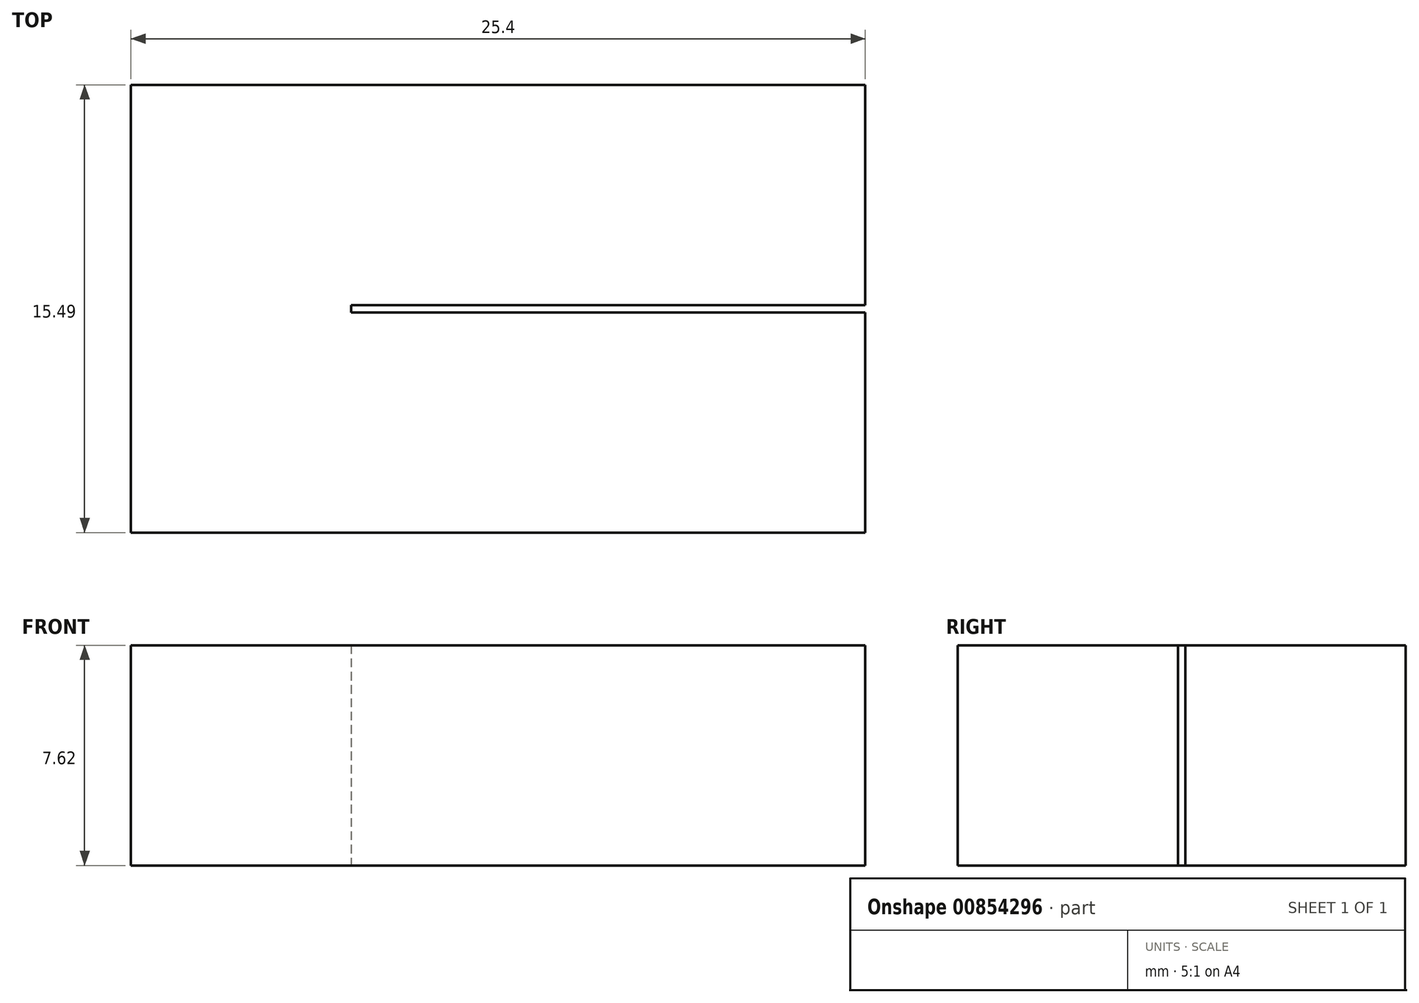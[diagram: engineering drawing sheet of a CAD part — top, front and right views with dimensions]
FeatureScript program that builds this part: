
annotation { "Feature Type Name" : "Feature", "Feature Type Description" : "" }
export const myFeature = defineFeature(function(context is Context, id is Id, definition is map)
    precondition{}
    {
        {
            var Q0;
            Q0=qCreatedBy(makeId("Top.planeOp"),FACE);
            var sketch = newSketch(context, id + "F0", { "sketchPlane" : qUnion([Q0])});
            skLineSegment(sketch, "E0", {"start": v(0, 0) * mm, "end": v(17.78, 0) * mm});
            skLineSegment(sketch, "E1", {"start": v(17.78, 0) * mm, "end": v(17.78, -7.62) * mm});
            skLineSegment(sketch, "E2", {"start": v(17.78, -7.62) * mm, "end": v(0, -7.62) * mm});
            skLineSegment(sketch, "E3", {"start": v(0, -7.62) * mm, "end": v(0, -7.87) * mm});
            skLineSegment(sketch, "E4", {"start": v(0, -7.87) * mm, "end": v(17.78, -7.87) * mm});
            skLineSegment(sketch, "E5", {"start": v(17.78, -7.87) * mm, "end": v(17.78, -15.5) * mm});
            skLineSegment(sketch, "E6", {"start": v(17.78, -15.5) * mm, "end": v(-7.62, -15.5) * mm});
            skLineSegment(sketch, "E7", {"start": v(-7.62, -15.5) * mm, "end": v(-7.62, 0) * mm});
            skLineSegment(sketch, "E8", {"start": v(-7.62, 0) * mm, "end": v(0, 0) * mm});
            skSolve(sketch);
        }
        {
            var Q0;
            Q0=makeQuery(id+"F0.imprint","IMPRINT",FACE,{"disambiguationData":[TD([[makeQuery(id+"F0.imprint","IMPRINT",EDGE,{"derivedFrom":sQuery(id+"F0.wireOp",EDGE,"E0")}),-1.0]])]});
            extrude(context, id + "F1", {"entities" : qUnion([Q0]), "depth" : 7.62 * mm, "offsetDistance" : 25.4 * mm});
        }
    });
